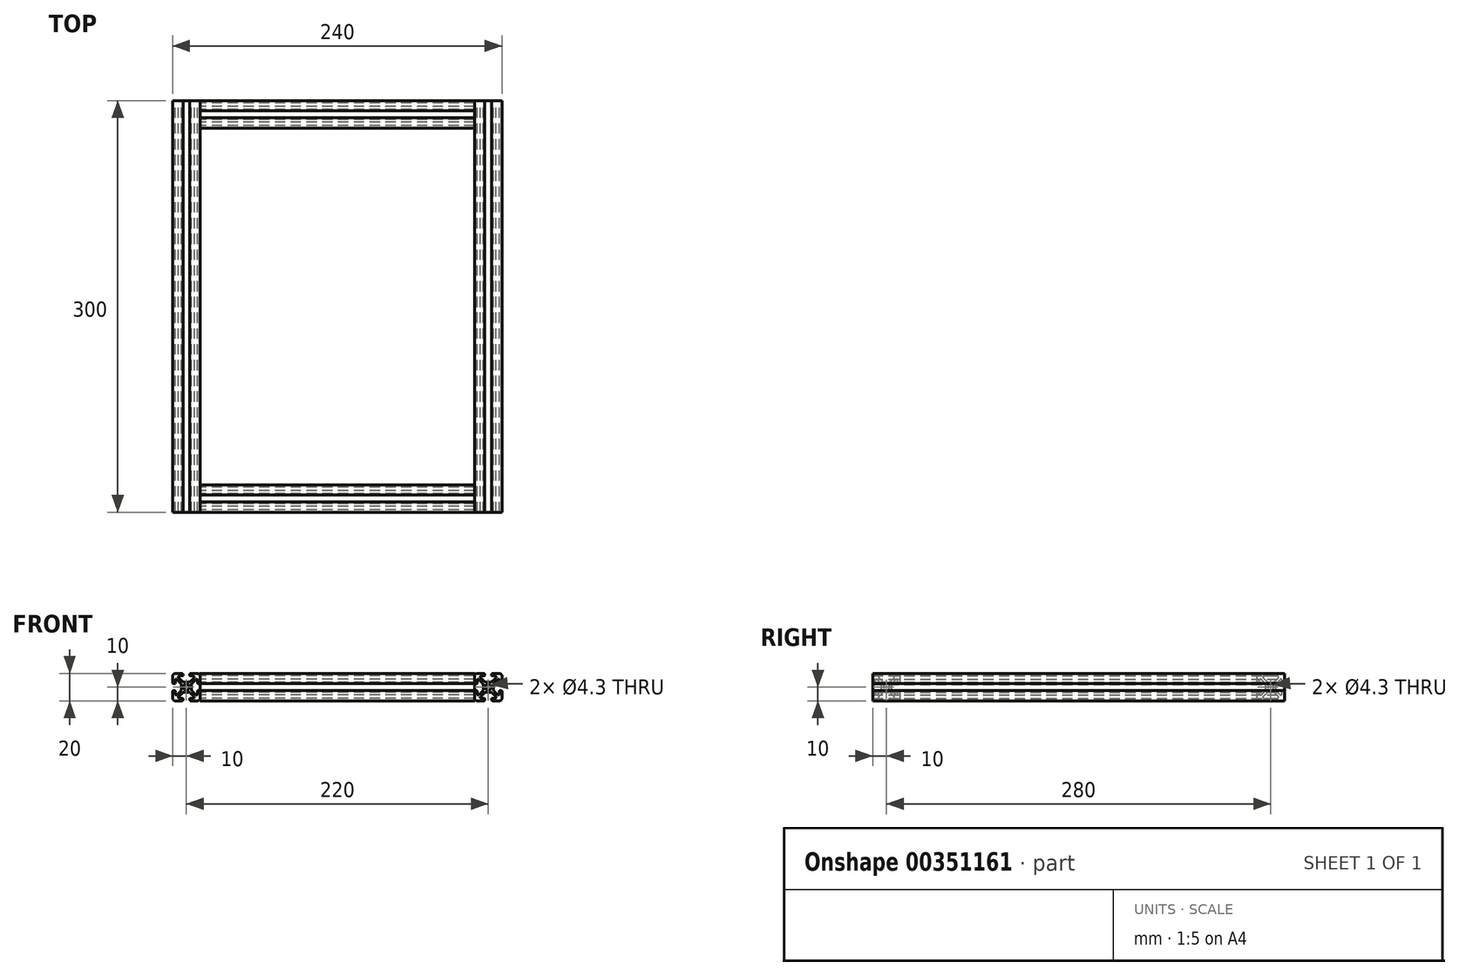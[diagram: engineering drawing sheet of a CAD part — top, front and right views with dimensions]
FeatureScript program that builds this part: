
annotation { "Feature Type Name" : "Feature", "Feature Type Description" : "" }
export const myFeature = defineFeature(function(context is Context, id is Id, definition is map)
    precondition{}
    {
        {
            var Q0;
            Q0=qCreatedBy(makeId("Front.planeOp"),FACE);
            var sketch = newSketch(context, id + "F0", { "sketchPlane" : qUnion([Q0])});
            skLineSegment(sketch, "E0", {"start": v(-103.22, -5.5) * mm, "end": v(-105.47, -3.26) * mm});
            skLineSegment(sketch, "E1", {"start": v(-114.53, 3.26) * mm, "end": v(-116.78, 5.5) * mm});
            skLineSegment(sketch, "E2", {"start": v(-104.5, -6.78) * mm, "end": v(-106.74, -4.53) * mm});
            skLineSegment(sketch, "E3", {"start": v(-113.26, 4.53) * mm, "end": v(-115.5, 6.78) * mm});
            skLineSegment(sketch, "E4", {"start": v(-106.7, -10) * mm, "end": v(-102, -10) * mm});
            skLineSegment(sketch, "E5", {"start": v(-118, -10) * mm, "end": v(-113.3, -10) * mm});
            skLineSegment(sketch, "E6", {"start": v(-114.92, -8.2) * mm, "end": v(-112.8, -8.2) * mm});
            skLineSegment(sketch, "E7", {"start": v(-107.2, -8.2) * mm, "end": v(-105.08, -8.2) * mm});
            skLineSegment(sketch, "E8", {"start": v(-111.13, -3.65) * mm, "end": v(-108.87, -3.65) * mm});
            skLineSegment(sketch, "E9", {"start": v(-101.5, -2.5) * mm, "end": v(-100.8, -2.5) * mm});
            skLineSegment(sketch, "E10", {"start": v(-119.2, -2.5) * mm, "end": v(-118.5, -2.5) * mm});
            skLineSegment(sketch, "E11", {"start": v(-101.5, 2.5) * mm, "end": v(-100.8, 2.5) * mm});
            skLineSegment(sketch, "E12", {"start": v(-119.2, 2.5) * mm, "end": v(-118.5, 2.5) * mm});
            skLineSegment(sketch, "E13", {"start": v(-111.13, 3.65) * mm, "end": v(-108.87, 3.65) * mm});
            skLineSegment(sketch, "E14", {"start": v(-107.2, 8.2) * mm, "end": v(-105.08, 8.2) * mm});
            skLineSegment(sketch, "E15", {"start": v(-114.92, 8.2) * mm, "end": v(-112.8, 8.2) * mm});
            skLineSegment(sketch, "E16", {"start": v(-106.7, 10) * mm, "end": v(-102, 10) * mm});
            skLineSegment(sketch, "E17", {"start": v(-118, 10) * mm, "end": v(-113.3, 10) * mm});
            skLineSegment(sketch, "E18", {"start": v(-105.47, 3.26) * mm, "end": v(-103.22, 5.5) * mm});
            skLineSegment(sketch, "E19", {"start": v(-115.5, -6.78) * mm, "end": v(-113.26, -4.53) * mm});
            skLineSegment(sketch, "E20", {"start": v(-106.74, 4.53) * mm, "end": v(-104.5, 6.78) * mm});
            skLineSegment(sketch, "E21", {"start": v(-116.78, -5.5) * mm, "end": v(-114.53, -3.26) * mm});
            skLineSegment(sketch, "E22", {"start": v(-120, 3.3) * mm, "end": v(-120, 8) * mm});
            skLineSegment(sketch, "E23", {"start": v(-120, -8) * mm, "end": v(-120, -3.3) * mm});
            skLineSegment(sketch, "E24", {"start": v(-118.2, 2.8) * mm, "end": v(-118.2, 4.92) * mm});
            skLineSegment(sketch, "E25", {"start": v(-118.2, -4.92) * mm, "end": v(-118.2, -2.8) * mm});
            skLineSegment(sketch, "E26", {"start": v(-113.65, -1.13) * mm, "end": v(-113.65, 1.13) * mm});
            skLineSegment(sketch, "E27", {"start": v(-112.5, 8.5) * mm, "end": v(-112.5, 9.2) * mm});
            skLineSegment(sketch, "E28", {"start": v(-112.5, -9.2) * mm, "end": v(-112.5, -8.5) * mm});
            skLineSegment(sketch, "E29", {"start": v(-107.5, -9.2) * mm, "end": v(-107.5, -8.5) * mm});
            skLineSegment(sketch, "E30", {"start": v(-107.5, 8.5) * mm, "end": v(-107.5, 9.2) * mm});
            skLineSegment(sketch, "E31", {"start": v(-106.35, -1.13) * mm, "end": v(-106.35, 1.13) * mm});
            skLineSegment(sketch, "E32", {"start": v(-101.8, -4.92) * mm, "end": v(-101.8, -2.8) * mm});
            skLineSegment(sketch, "E33", {"start": v(-101.8, 2.8) * mm, "end": v(-101.8, 4.92) * mm});
            skLineSegment(sketch, "E34", {"start": v(-100, -8) * mm, "end": v(-100, -3.3) * mm});
            skLineSegment(sketch, "E35", {"start": v(-100, 3.3) * mm, "end": v(-100, 8) * mm});
            skArc(sketch, "E36", {"start": v(-119.2, -2.5) * mm, "mid": v(-119.77, -2.73) * mm, "end": v(-120, -3.3) * mm});
            skArc(sketch, "E37", {"start": v(-120, 3.3) * mm, "mid": v(-119.77, 2.73) * mm, "end": v(-119.2, 2.5) * mm});
            skArc(sketch, "E38", {"start": v(-118.2, -2.8) * mm, "mid": v(-118.29, -2.59) * mm, "end": v(-118.5, -2.5) * mm});
            skArc(sketch, "E39", {"start": v(-118.5, 2.5) * mm, "mid": v(-118.29, 2.59) * mm, "end": v(-118.2, 2.8) * mm});
            skArc(sketch, "E40", {"start": v(-120, -8) * mm, "mid": v(-119.41, -9.41) * mm, "end": v(-118, -10) * mm});
            skArc(sketch, "E41", {"start": v(-118, 10) * mm, "mid": v(-119.41, 9.41) * mm, "end": v(-120, 8) * mm});
            skArc(sketch, "E42", {"start": v(-118.2, -4.92) * mm, "mid": v(-117.69, -5.69) * mm, "end": v(-116.78, -5.5) * mm});
            skArc(sketch, "E43", {"start": v(-116.78, 5.5) * mm, "mid": v(-117.69, 5.69) * mm, "end": v(-118.2, 4.92) * mm});
            skArc(sketch, "E44", {"start": v(-114.53, -3.26) * mm, "mid": v(-113.88, -2.28) * mm, "end": v(-113.65, -1.13) * mm});
            skArc(sketch, "E45", {"start": v(-113.65, 1.13) * mm, "mid": v(-113.88, 2.28) * mm, "end": v(-114.53, 3.26) * mm});
            skArc(sketch, "E46", {"start": v(-115.5, -6.78) * mm, "mid": v(-115.69, -7.69) * mm, "end": v(-114.92, -8.2) * mm});
            skArc(sketch, "E47", {"start": v(-114.92, 8.2) * mm, "mid": v(-115.69, 7.69) * mm, "end": v(-115.5, 6.78) * mm});
            skArc(sketch, "E48", {"start": v(-113.3, -10) * mm, "mid": v(-112.73, -9.77) * mm, "end": v(-112.5, -9.2) * mm});
            skArc(sketch, "E49", {"start": v(-112.5, 9.2) * mm, "mid": v(-112.73, 9.77) * mm, "end": v(-113.3, 10) * mm});
            skArc(sketch, "E50", {"start": v(-112.5, -8.5) * mm, "mid": v(-112.59, -8.29) * mm, "end": v(-112.8, -8.2) * mm});
            skArc(sketch, "E51", {"start": v(-112.8, 8.2) * mm, "mid": v(-112.59, 8.29) * mm, "end": v(-112.5, 8.5) * mm});
            skArc(sketch, "E52", {"start": v(-111.13, -3.65) * mm, "mid": v(-112.28, -3.88) * mm, "end": v(-113.26, -4.53) * mm});
            skArc(sketch, "E53", {"start": v(-113.26, 4.53) * mm, "mid": v(-112.28, 3.88) * mm, "end": v(-111.13, 3.65) * mm});
            skCircle(sketch, "E54", {"center": v(-110, 0) * mm, "radius": 2.15 * mm});
            skArc(sketch, "E55", {"start": v(-106.74, -4.53) * mm, "mid": v(-107.72, -3.88) * mm, "end": v(-108.87, -3.65) * mm});
            skArc(sketch, "E56", {"start": v(-108.87, 3.65) * mm, "mid": v(-107.72, 3.88) * mm, "end": v(-106.74, 4.53) * mm});
            skArc(sketch, "E57", {"start": v(-107.2, -8.2) * mm, "mid": v(-107.41, -8.29) * mm, "end": v(-107.5, -8.5) * mm});
            skArc(sketch, "E58", {"start": v(-107.5, 8.5) * mm, "mid": v(-107.41, 8.29) * mm, "end": v(-107.2, 8.2) * mm});
            skArc(sketch, "E59", {"start": v(-107.5, -9.2) * mm, "mid": v(-107.27, -9.77) * mm, "end": v(-106.7, -10) * mm});
            skArc(sketch, "E60", {"start": v(-106.7, 10) * mm, "mid": v(-107.27, 9.77) * mm, "end": v(-107.5, 9.2) * mm});
            skArc(sketch, "E61", {"start": v(-105.08, -8.2) * mm, "mid": v(-104.31, -7.69) * mm, "end": v(-104.5, -6.78) * mm});
            skArc(sketch, "E62", {"start": v(-104.5, 6.78) * mm, "mid": v(-104.31, 7.69) * mm, "end": v(-105.08, 8.2) * mm});
            skArc(sketch, "E63", {"start": v(-106.35, -1.13) * mm, "mid": v(-106.12, -2.28) * mm, "end": v(-105.47, -3.26) * mm});
            skArc(sketch, "E64", {"start": v(-105.47, 3.26) * mm, "mid": v(-106.12, 2.28) * mm, "end": v(-106.35, 1.13) * mm});
            skArc(sketch, "E65", {"start": v(-103.22, -5.5) * mm, "mid": v(-102.31, -5.69) * mm, "end": v(-101.8, -4.92) * mm});
            skArc(sketch, "E66", {"start": v(-101.8, 4.92) * mm, "mid": v(-102.31, 5.69) * mm, "end": v(-103.22, 5.5) * mm});
            skArc(sketch, "E67", {"start": v(-102, -10) * mm, "mid": v(-100.59, -9.41) * mm, "end": v(-100, -8) * mm});
            skArc(sketch, "E68", {"start": v(-100, 8) * mm, "mid": v(-100.59, 9.41) * mm, "end": v(-102, 10) * mm});
            skArc(sketch, "E69", {"start": v(-101.5, -2.5) * mm, "mid": v(-101.71, -2.59) * mm, "end": v(-101.8, -2.8) * mm});
            skArc(sketch, "E70", {"start": v(-101.8, 2.8) * mm, "mid": v(-101.71, 2.59) * mm, "end": v(-101.5, 2.5) * mm});
            skArc(sketch, "E71", {"start": v(-100, -3.3) * mm, "mid": v(-100.23, -2.73) * mm, "end": v(-100.8, -2.5) * mm});
            skArc(sketch, "E72", {"start": v(-100.8, 2.5) * mm, "mid": v(-100.23, 2.73) * mm, "end": v(-100, 3.3) * mm});
            skLineSegment(sketch, "E73", {"start": v(-110, 10) * mm, "end": v(-110, -10) * mm});
            skLineSegment(sketch, "E74", {"start": v(-120, 0) * mm, "end": v(-100, 0) * mm});
            skLineSegment(sketch, "E75", {"start": v(116.78, -5.5) * mm, "end": v(114.53, -3.26) * mm});
            skLineSegment(sketch, "E76", {"start": v(105.47, 3.26) * mm, "end": v(103.22, 5.5) * mm});
            skLineSegment(sketch, "E77", {"start": v(115.5, -6.78) * mm, "end": v(113.26, -4.53) * mm});
            skLineSegment(sketch, "E78", {"start": v(106.74, 4.53) * mm, "end": v(104.5, 6.78) * mm});
            skLineSegment(sketch, "E79", {"start": v(113.3, -10) * mm, "end": v(118, -10) * mm});
            skLineSegment(sketch, "E80", {"start": v(102, -10) * mm, "end": v(106.7, -10) * mm});
            skLineSegment(sketch, "E81", {"start": v(105.08, -8.2) * mm, "end": v(107.2, -8.2) * mm});
            skLineSegment(sketch, "E82", {"start": v(112.8, -8.2) * mm, "end": v(114.92, -8.2) * mm});
            skLineSegment(sketch, "E83", {"start": v(108.87, -3.65) * mm, "end": v(111.13, -3.65) * mm});
            skLineSegment(sketch, "E84", {"start": v(118.5, -2.5) * mm, "end": v(119.2, -2.5) * mm});
            skLineSegment(sketch, "E85", {"start": v(100.8, -2.5) * mm, "end": v(101.5, -2.5) * mm});
            skLineSegment(sketch, "E86", {"start": v(118.5, 2.5) * mm, "end": v(119.2, 2.5) * mm});
            skLineSegment(sketch, "E87", {"start": v(100.8, 2.5) * mm, "end": v(101.5, 2.5) * mm});
            skLineSegment(sketch, "E88", {"start": v(108.87, 3.65) * mm, "end": v(111.13, 3.65) * mm});
            skLineSegment(sketch, "E89", {"start": v(112.8, 8.2) * mm, "end": v(114.92, 8.2) * mm});
            skLineSegment(sketch, "E90", {"start": v(105.08, 8.2) * mm, "end": v(107.2, 8.2) * mm});
            skLineSegment(sketch, "E91", {"start": v(113.3, 10) * mm, "end": v(118, 10) * mm});
            skLineSegment(sketch, "E92", {"start": v(102, 10) * mm, "end": v(106.7, 10) * mm});
            skLineSegment(sketch, "E93", {"start": v(114.53, 3.26) * mm, "end": v(116.78, 5.5) * mm});
            skLineSegment(sketch, "E94", {"start": v(104.5, -6.78) * mm, "end": v(106.74, -4.53) * mm});
            skLineSegment(sketch, "E95", {"start": v(113.26, 4.53) * mm, "end": v(115.5, 6.78) * mm});
            skLineSegment(sketch, "E96", {"start": v(103.22, -5.5) * mm, "end": v(105.47, -3.26) * mm});
            skLineSegment(sketch, "E97", {"start": v(100, 3.3) * mm, "end": v(100, 8) * mm});
            skLineSegment(sketch, "E98", {"start": v(100, -8) * mm, "end": v(100, -3.3) * mm});
            skLineSegment(sketch, "E99", {"start": v(101.8, 2.8) * mm, "end": v(101.8, 4.92) * mm});
            skLineSegment(sketch, "E100", {"start": v(101.8, -4.92) * mm, "end": v(101.8, -2.8) * mm});
            skLineSegment(sketch, "E101", {"start": v(106.35, -1.13) * mm, "end": v(106.35, 1.13) * mm});
            skLineSegment(sketch, "E102", {"start": v(107.5, 8.5) * mm, "end": v(107.5, 9.2) * mm});
            skLineSegment(sketch, "E103", {"start": v(107.5, -9.2) * mm, "end": v(107.5, -8.5) * mm});
            skLineSegment(sketch, "E104", {"start": v(112.5, -9.2) * mm, "end": v(112.5, -8.5) * mm});
            skLineSegment(sketch, "E105", {"start": v(112.5, 8.5) * mm, "end": v(112.5, 9.2) * mm});
            skLineSegment(sketch, "E106", {"start": v(113.65, -1.13) * mm, "end": v(113.65, 1.13) * mm});
            skLineSegment(sketch, "E107", {"start": v(118.2, -4.92) * mm, "end": v(118.2, -2.8) * mm});
            skLineSegment(sketch, "E108", {"start": v(118.2, 2.8) * mm, "end": v(118.2, 4.92) * mm});
            skLineSegment(sketch, "E109", {"start": v(120, -8) * mm, "end": v(120, -3.3) * mm});
            skLineSegment(sketch, "E110", {"start": v(120, 3.3) * mm, "end": v(120, 8) * mm});
            skArc(sketch, "E111", {"start": v(100.8, -2.5) * mm, "mid": v(100.23, -2.73) * mm, "end": v(100, -3.3) * mm});
            skArc(sketch, "E112", {"start": v(100, 3.3) * mm, "mid": v(100.23, 2.73) * mm, "end": v(100.8, 2.5) * mm});
            skArc(sketch, "E113", {"start": v(101.8, -2.8) * mm, "mid": v(101.71, -2.59) * mm, "end": v(101.5, -2.5) * mm});
            skArc(sketch, "E114", {"start": v(101.5, 2.5) * mm, "mid": v(101.71, 2.59) * mm, "end": v(101.8, 2.8) * mm});
            skArc(sketch, "E115", {"start": v(100, -8) * mm, "mid": v(100.59, -9.41) * mm, "end": v(102, -10) * mm});
            skArc(sketch, "E116", {"start": v(102, 10) * mm, "mid": v(100.59, 9.41) * mm, "end": v(100, 8) * mm});
            skArc(sketch, "E117", {"start": v(101.8, -4.92) * mm, "mid": v(102.31, -5.69) * mm, "end": v(103.22, -5.5) * mm});
            skArc(sketch, "E118", {"start": v(103.22, 5.5) * mm, "mid": v(102.31, 5.69) * mm, "end": v(101.8, 4.92) * mm});
            skArc(sketch, "E119", {"start": v(105.47, -3.26) * mm, "mid": v(106.12, -2.28) * mm, "end": v(106.35, -1.13) * mm});
            skArc(sketch, "E120", {"start": v(106.35, 1.13) * mm, "mid": v(106.12, 2.28) * mm, "end": v(105.47, 3.26) * mm});
            skArc(sketch, "E121", {"start": v(104.5, -6.78) * mm, "mid": v(104.31, -7.69) * mm, "end": v(105.08, -8.2) * mm});
            skArc(sketch, "E122", {"start": v(105.08, 8.2) * mm, "mid": v(104.31, 7.69) * mm, "end": v(104.5, 6.78) * mm});
            skArc(sketch, "E123", {"start": v(106.7, -10) * mm, "mid": v(107.27, -9.77) * mm, "end": v(107.5, -9.2) * mm});
            skArc(sketch, "E124", {"start": v(107.5, 9.2) * mm, "mid": v(107.27, 9.77) * mm, "end": v(106.7, 10) * mm});
            skArc(sketch, "E125", {"start": v(107.5, -8.5) * mm, "mid": v(107.41, -8.29) * mm, "end": v(107.2, -8.2) * mm});
            skArc(sketch, "E126", {"start": v(107.2, 8.2) * mm, "mid": v(107.41, 8.29) * mm, "end": v(107.5, 8.5) * mm});
            skArc(sketch, "E127", {"start": v(108.87, -3.65) * mm, "mid": v(107.72, -3.88) * mm, "end": v(106.74, -4.53) * mm});
            skArc(sketch, "E128", {"start": v(106.74, 4.53) * mm, "mid": v(107.72, 3.88) * mm, "end": v(108.87, 3.65) * mm});
            skCircle(sketch, "E129", {"center": v(110, 0) * mm, "radius": 2.15 * mm});
            skArc(sketch, "E130", {"start": v(113.26, -4.53) * mm, "mid": v(112.28, -3.88) * mm, "end": v(111.13, -3.65) * mm});
            skArc(sketch, "E131", {"start": v(111.13, 3.65) * mm, "mid": v(112.28, 3.88) * mm, "end": v(113.26, 4.53) * mm});
            skArc(sketch, "E132", {"start": v(112.8, -8.2) * mm, "mid": v(112.59, -8.29) * mm, "end": v(112.5, -8.5) * mm});
            skArc(sketch, "E133", {"start": v(112.5, 8.5) * mm, "mid": v(112.59, 8.29) * mm, "end": v(112.8, 8.2) * mm});
            skArc(sketch, "E134", {"start": v(112.5, -9.2) * mm, "mid": v(112.73, -9.77) * mm, "end": v(113.3, -10) * mm});
            skArc(sketch, "E135", {"start": v(113.3, 10) * mm, "mid": v(112.73, 9.77) * mm, "end": v(112.5, 9.2) * mm});
            skArc(sketch, "E136", {"start": v(114.92, -8.2) * mm, "mid": v(115.69, -7.69) * mm, "end": v(115.5, -6.78) * mm});
            skArc(sketch, "E137", {"start": v(115.5, 6.78) * mm, "mid": v(115.69, 7.69) * mm, "end": v(114.92, 8.2) * mm});
            skArc(sketch, "E138", {"start": v(113.65, -1.13) * mm, "mid": v(113.88, -2.28) * mm, "end": v(114.53, -3.26) * mm});
            skArc(sketch, "E139", {"start": v(114.53, 3.26) * mm, "mid": v(113.88, 2.28) * mm, "end": v(113.65, 1.13) * mm});
            skArc(sketch, "E140", {"start": v(116.78, -5.5) * mm, "mid": v(117.69, -5.69) * mm, "end": v(118.2, -4.92) * mm});
            skArc(sketch, "E141", {"start": v(118.2, 4.92) * mm, "mid": v(117.69, 5.69) * mm, "end": v(116.78, 5.5) * mm});
            skArc(sketch, "E142", {"start": v(118, -10) * mm, "mid": v(119.41, -9.41) * mm, "end": v(120, -8) * mm});
            skArc(sketch, "E143", {"start": v(120, 8) * mm, "mid": v(119.41, 9.41) * mm, "end": v(118, 10) * mm});
            skArc(sketch, "E144", {"start": v(118.5, -2.5) * mm, "mid": v(118.29, -2.59) * mm, "end": v(118.2, -2.8) * mm});
            skArc(sketch, "E145", {"start": v(118.2, 2.8) * mm, "mid": v(118.29, 2.59) * mm, "end": v(118.5, 2.5) * mm});
            skArc(sketch, "E146", {"start": v(120, -3.3) * mm, "mid": v(119.77, -2.73) * mm, "end": v(119.2, -2.5) * mm});
            skArc(sketch, "E147", {"start": v(119.2, 2.5) * mm, "mid": v(119.77, 2.73) * mm, "end": v(120, 3.3) * mm});
            skLineSegment(sketch, "E148", {"start": v(110, 10) * mm, "end": v(110, -10) * mm});
            skLineSegment(sketch, "E149", {"start": v(100, 0) * mm, "end": v(120, 0) * mm});
            skSolve(sketch);
        }
        {
            var Q0;
            Q0=makeQuery(id+"F0.imprint","IMPRINT",FACE,{"disambiguationData":[TD([[makeQuery(id+"F0.imprint","IMPRINT",EDGE,{"derivedFrom":sQuery(id+"F0.wireOp",EDGE,"E1")}),-1.0]])]});
            var Q1;
            Q1=makeQuery(id+"F0.imprint","IMPRINT",FACE,{"disambiguationData":[TD([[makeQuery(id+"F0.imprint","IMPRINT",EDGE,{"derivedFrom":sQuery(id+"F0.wireOp",EDGE,"E11")}),1.0]])]});
            var Q2;
            Q2=makeQuery(id+"F0.imprint","IMPRINT",FACE,{"disambiguationData":[TD([[makeQuery(id+"F0.imprint","IMPRINT",EDGE,{"derivedFrom":sQuery(id+"F0.wireOp",EDGE,"E5")}),1.0]])]});
            var Q3;
            Q3=makeQuery(id+"F0.imprint","IMPRINT",FACE,{"disambiguationData":[TD([[makeQuery(id+"F0.imprint","IMPRINT",EDGE,{"derivedFrom":sQuery(id+"F0.wireOp",EDGE,"E0")}),1.0]])]});
            var Q4;
            Q4=makeQuery(id+"F0.imprint","IMPRINT",FACE,{"disambiguationData":[TD([[makeQuery(id+"F0.imprint","IMPRINT",EDGE,{"derivedFrom":sQuery(id+"F0.wireOp",EDGE,"E76")}),-1.0]])]});
            var Q5;
            Q5=makeQuery(id+"F0.imprint","IMPRINT",FACE,{"disambiguationData":[TD([[makeQuery(id+"F0.imprint","IMPRINT",EDGE,{"derivedFrom":sQuery(id+"F0.wireOp",EDGE,"E86")}),1.0]])]});
            var Q6;
            Q6=makeQuery(id+"F0.imprint","IMPRINT",FACE,{"disambiguationData":[TD([[makeQuery(id+"F0.imprint","IMPRINT",EDGE,{"derivedFrom":sQuery(id+"F0.wireOp",EDGE,"E75")}),1.0]])]});
            var Q7;
            Q7=makeQuery(id+"F0.imprint","IMPRINT",FACE,{"disambiguationData":[TD([[makeQuery(id+"F0.imprint","IMPRINT",EDGE,{"derivedFrom":sQuery(id+"F0.wireOp",EDGE,"E80")}),1.0]])]});
            extrude(context, id + "F1", {"entities" : qUnion([Q0, Q1, Q2, Q3, Q4, Q5, Q6, Q7]), "endBound" : BoundingType.SYMMETRIC, "depth" : 300 * mm});
        }
        {
            var Q0;
            Q0=qCreatedBy(makeId("Right.planeOp"),FACE);
            var sketch = newSketch(context, id + "F2", { "sketchPlane" : qUnion([Q0])});
            skLineSegment(sketch, "E150", {"start": v(-133.22, -5.5) * mm, "end": v(-135.47, -3.26) * mm});
            skLineSegment(sketch, "E151", {"start": v(-144.53, 3.26) * mm, "end": v(-146.78, 5.5) * mm});
            skLineSegment(sketch, "E152", {"start": v(-134.5, -6.78) * mm, "end": v(-136.74, -4.53) * mm});
            skLineSegment(sketch, "E153", {"start": v(-143.26, 4.53) * mm, "end": v(-145.5, 6.78) * mm});
            skLineSegment(sketch, "E154", {"start": v(-136.7, -10) * mm, "end": v(-132, -10) * mm});
            skLineSegment(sketch, "E155", {"start": v(-148, -10) * mm, "end": v(-143.3, -10) * mm});
            skLineSegment(sketch, "E156", {"start": v(-144.92, -8.2) * mm, "end": v(-142.8, -8.2) * mm});
            skLineSegment(sketch, "E157", {"start": v(-137.2, -8.2) * mm, "end": v(-135.08, -8.2) * mm});
            skLineSegment(sketch, "E158", {"start": v(-141.13, -3.65) * mm, "end": v(-138.87, -3.65) * mm});
            skLineSegment(sketch, "E159", {"start": v(-131.5, -2.5) * mm, "end": v(-130.8, -2.5) * mm});
            skLineSegment(sketch, "E160", {"start": v(-149.2, -2.5) * mm, "end": v(-148.5, -2.5) * mm});
            skLineSegment(sketch, "E161", {"start": v(-131.5, 2.5) * mm, "end": v(-130.8, 2.5) * mm});
            skLineSegment(sketch, "E162", {"start": v(-149.2, 2.5) * mm, "end": v(-148.5, 2.5) * mm});
            skLineSegment(sketch, "E163", {"start": v(-141.13, 3.65) * mm, "end": v(-138.87, 3.65) * mm});
            skLineSegment(sketch, "E164", {"start": v(-137.2, 8.2) * mm, "end": v(-135.08, 8.2) * mm});
            skLineSegment(sketch, "E165", {"start": v(-144.92, 8.2) * mm, "end": v(-142.8, 8.2) * mm});
            skLineSegment(sketch, "E166", {"start": v(-136.7, 10) * mm, "end": v(-132, 10) * mm});
            skLineSegment(sketch, "E167", {"start": v(-148, 10) * mm, "end": v(-143.3, 10) * mm});
            skLineSegment(sketch, "E168", {"start": v(-135.47, 3.26) * mm, "end": v(-133.22, 5.5) * mm});
            skLineSegment(sketch, "E169", {"start": v(-145.5, -6.78) * mm, "end": v(-143.26, -4.53) * mm});
            skLineSegment(sketch, "E170", {"start": v(-136.74, 4.53) * mm, "end": v(-134.5, 6.78) * mm});
            skLineSegment(sketch, "E171", {"start": v(-146.78, -5.5) * mm, "end": v(-144.53, -3.26) * mm});
            skLineSegment(sketch, "E172", {"start": v(-150, 3.3) * mm, "end": v(-150, 8) * mm});
            skLineSegment(sketch, "E173", {"start": v(-150, -8) * mm, "end": v(-150, -3.3) * mm});
            skLineSegment(sketch, "E174", {"start": v(-148.2, 2.8) * mm, "end": v(-148.2, 4.92) * mm});
            skLineSegment(sketch, "E175", {"start": v(-148.2, -4.92) * mm, "end": v(-148.2, -2.8) * mm});
            skLineSegment(sketch, "E176", {"start": v(-143.65, -1.13) * mm, "end": v(-143.65, 1.13) * mm});
            skLineSegment(sketch, "E177", {"start": v(-142.5, 8.5) * mm, "end": v(-142.5, 9.2) * mm});
            skLineSegment(sketch, "E178", {"start": v(-142.5, -9.2) * mm, "end": v(-142.5, -8.5) * mm});
            skLineSegment(sketch, "E179", {"start": v(-137.5, -9.2) * mm, "end": v(-137.5, -8.5) * mm});
            skLineSegment(sketch, "E180", {"start": v(-137.5, 8.5) * mm, "end": v(-137.5, 9.2) * mm});
            skLineSegment(sketch, "E181", {"start": v(-136.35, -1.13) * mm, "end": v(-136.35, 1.13) * mm});
            skLineSegment(sketch, "E182", {"start": v(-131.8, -4.92) * mm, "end": v(-131.8, -2.8) * mm});
            skLineSegment(sketch, "E183", {"start": v(-131.8, 2.8) * mm, "end": v(-131.8, 4.92) * mm});
            skLineSegment(sketch, "E184", {"start": v(-130, -8) * mm, "end": v(-130, -3.3) * mm});
            skLineSegment(sketch, "E185", {"start": v(-130, 3.3) * mm, "end": v(-130, 8) * mm});
            skArc(sketch, "E186", {"start": v(-149.2, -2.5) * mm, "mid": v(-149.77, -2.73) * mm, "end": v(-150, -3.3) * mm});
            skArc(sketch, "E187", {"start": v(-150, 3.3) * mm, "mid": v(-149.77, 2.73) * mm, "end": v(-149.2, 2.5) * mm});
            skArc(sketch, "E188", {"start": v(-148.2, -2.8) * mm, "mid": v(-148.29, -2.59) * mm, "end": v(-148.5, -2.5) * mm});
            skArc(sketch, "E189", {"start": v(-148.5, 2.5) * mm, "mid": v(-148.29, 2.59) * mm, "end": v(-148.2, 2.8) * mm});
            skArc(sketch, "E190", {"start": v(-150, -8) * mm, "mid": v(-149.41, -9.41) * mm, "end": v(-148, -10) * mm});
            skArc(sketch, "E191", {"start": v(-148, 10) * mm, "mid": v(-149.41, 9.41) * mm, "end": v(-150, 8) * mm});
            skArc(sketch, "E192", {"start": v(-148.2, -4.92) * mm, "mid": v(-147.69, -5.69) * mm, "end": v(-146.78, -5.5) * mm});
            skArc(sketch, "E193", {"start": v(-146.78, 5.5) * mm, "mid": v(-147.69, 5.69) * mm, "end": v(-148.2, 4.92) * mm});
            skArc(sketch, "E194", {"start": v(-144.53, -3.26) * mm, "mid": v(-143.88, -2.28) * mm, "end": v(-143.65, -1.13) * mm});
            skArc(sketch, "E195", {"start": v(-143.65, 1.13) * mm, "mid": v(-143.88, 2.28) * mm, "end": v(-144.53, 3.26) * mm});
            skArc(sketch, "E196", {"start": v(-145.5, -6.78) * mm, "mid": v(-145.69, -7.69) * mm, "end": v(-144.92, -8.2) * mm});
            skArc(sketch, "E197", {"start": v(-144.92, 8.2) * mm, "mid": v(-145.69, 7.69) * mm, "end": v(-145.5, 6.78) * mm});
            skArc(sketch, "E198", {"start": v(-143.3, -10) * mm, "mid": v(-142.73, -9.77) * mm, "end": v(-142.5, -9.2) * mm});
            skArc(sketch, "E199", {"start": v(-142.5, 9.2) * mm, "mid": v(-142.73, 9.77) * mm, "end": v(-143.3, 10) * mm});
            skArc(sketch, "E200", {"start": v(-142.5, -8.5) * mm, "mid": v(-142.59, -8.29) * mm, "end": v(-142.8, -8.2) * mm});
            skArc(sketch, "E201", {"start": v(-142.8, 8.2) * mm, "mid": v(-142.59, 8.29) * mm, "end": v(-142.5, 8.5) * mm});
            skArc(sketch, "E202", {"start": v(-141.13, -3.65) * mm, "mid": v(-142.28, -3.88) * mm, "end": v(-143.26, -4.53) * mm});
            skArc(sketch, "E203", {"start": v(-143.26, 4.53) * mm, "mid": v(-142.28, 3.88) * mm, "end": v(-141.13, 3.65) * mm});
            skCircle(sketch, "E204", {"center": v(-140, 0) * mm, "radius": 2.15 * mm});
            skArc(sketch, "E205", {"start": v(-136.74, -4.53) * mm, "mid": v(-137.72, -3.88) * mm, "end": v(-138.87, -3.65) * mm});
            skArc(sketch, "E206", {"start": v(-138.87, 3.65) * mm, "mid": v(-137.72, 3.88) * mm, "end": v(-136.74, 4.53) * mm});
            skArc(sketch, "E207", {"start": v(-137.2, -8.2) * mm, "mid": v(-137.41, -8.29) * mm, "end": v(-137.5, -8.5) * mm});
            skArc(sketch, "E208", {"start": v(-137.5, 8.5) * mm, "mid": v(-137.41, 8.29) * mm, "end": v(-137.2, 8.2) * mm});
            skArc(sketch, "E209", {"start": v(-137.5, -9.2) * mm, "mid": v(-137.27, -9.77) * mm, "end": v(-136.7, -10) * mm});
            skArc(sketch, "E210", {"start": v(-136.7, 10) * mm, "mid": v(-137.27, 9.77) * mm, "end": v(-137.5, 9.2) * mm});
            skArc(sketch, "E211", {"start": v(-135.08, -8.2) * mm, "mid": v(-134.31, -7.69) * mm, "end": v(-134.5, -6.78) * mm});
            skArc(sketch, "E212", {"start": v(-134.5, 6.78) * mm, "mid": v(-134.31, 7.69) * mm, "end": v(-135.08, 8.2) * mm});
            skArc(sketch, "E213", {"start": v(-136.35, -1.13) * mm, "mid": v(-136.12, -2.28) * mm, "end": v(-135.47, -3.26) * mm});
            skArc(sketch, "E214", {"start": v(-135.47, 3.26) * mm, "mid": v(-136.12, 2.28) * mm, "end": v(-136.35, 1.13) * mm});
            skArc(sketch, "E215", {"start": v(-133.22, -5.5) * mm, "mid": v(-132.31, -5.69) * mm, "end": v(-131.8, -4.92) * mm});
            skArc(sketch, "E216", {"start": v(-131.8, 4.92) * mm, "mid": v(-132.31, 5.69) * mm, "end": v(-133.22, 5.5) * mm});
            skArc(sketch, "E217", {"start": v(-132, -10) * mm, "mid": v(-130.59, -9.41) * mm, "end": v(-130, -8) * mm});
            skArc(sketch, "E218", {"start": v(-130, 8) * mm, "mid": v(-130.59, 9.41) * mm, "end": v(-132, 10) * mm});
            skArc(sketch, "E219", {"start": v(-131.5, -2.5) * mm, "mid": v(-131.71, -2.59) * mm, "end": v(-131.8, -2.8) * mm});
            skArc(sketch, "E220", {"start": v(-131.8, 2.8) * mm, "mid": v(-131.71, 2.59) * mm, "end": v(-131.5, 2.5) * mm});
            skArc(sketch, "E221", {"start": v(-130, -3.3) * mm, "mid": v(-130.23, -2.73) * mm, "end": v(-130.8, -2.5) * mm});
            skArc(sketch, "E222", {"start": v(-130.8, 2.5) * mm, "mid": v(-130.23, 2.73) * mm, "end": v(-130, 3.3) * mm});
            skLineSegment(sketch, "E223", {"start": v(-140, 10) * mm, "end": v(-140, -10) * mm});
            skLineSegment(sketch, "E224", {"start": v(-150, 0) * mm, "end": v(-130, 0) * mm});
            skLineSegment(sketch, "E225", {"start": v(146.78, -5.5) * mm, "end": v(144.53, -3.26) * mm});
            skLineSegment(sketch, "E226", {"start": v(135.47, 3.26) * mm, "end": v(133.22, 5.5) * mm});
            skLineSegment(sketch, "E227", {"start": v(145.5, -6.78) * mm, "end": v(143.26, -4.53) * mm});
            skLineSegment(sketch, "E228", {"start": v(136.74, 4.53) * mm, "end": v(134.5, 6.78) * mm});
            skLineSegment(sketch, "E229", {"start": v(143.3, -10) * mm, "end": v(148, -10) * mm});
            skLineSegment(sketch, "E230", {"start": v(132, -10) * mm, "end": v(136.7, -10) * mm});
            skLineSegment(sketch, "E231", {"start": v(135.08, -8.2) * mm, "end": v(137.2, -8.2) * mm});
            skLineSegment(sketch, "E232", {"start": v(142.8, -8.2) * mm, "end": v(144.92, -8.2) * mm});
            skLineSegment(sketch, "E233", {"start": v(138.87, -3.65) * mm, "end": v(141.13, -3.65) * mm});
            skLineSegment(sketch, "E234", {"start": v(148.5, -2.5) * mm, "end": v(149.2, -2.5) * mm});
            skLineSegment(sketch, "E235", {"start": v(130.8, -2.5) * mm, "end": v(131.5, -2.5) * mm});
            skLineSegment(sketch, "E236", {"start": v(148.5, 2.5) * mm, "end": v(149.2, 2.5) * mm});
            skLineSegment(sketch, "E237", {"start": v(130.8, 2.5) * mm, "end": v(131.5, 2.5) * mm});
            skLineSegment(sketch, "E238", {"start": v(138.87, 3.65) * mm, "end": v(141.13, 3.65) * mm});
            skLineSegment(sketch, "E239", {"start": v(142.8, 8.2) * mm, "end": v(144.92, 8.2) * mm});
            skLineSegment(sketch, "E240", {"start": v(135.08, 8.2) * mm, "end": v(137.2, 8.2) * mm});
            skLineSegment(sketch, "E241", {"start": v(143.3, 10) * mm, "end": v(148, 10) * mm});
            skLineSegment(sketch, "E242", {"start": v(132, 10) * mm, "end": v(136.7, 10) * mm});
            skLineSegment(sketch, "E243", {"start": v(144.53, 3.26) * mm, "end": v(146.78, 5.5) * mm});
            skLineSegment(sketch, "E244", {"start": v(134.5, -6.78) * mm, "end": v(136.74, -4.53) * mm});
            skLineSegment(sketch, "E245", {"start": v(143.26, 4.53) * mm, "end": v(145.5, 6.78) * mm});
            skLineSegment(sketch, "E246", {"start": v(133.22, -5.5) * mm, "end": v(135.47, -3.26) * mm});
            skLineSegment(sketch, "E247", {"start": v(130, 3.3) * mm, "end": v(130, 8) * mm});
            skLineSegment(sketch, "E248", {"start": v(130, -8) * mm, "end": v(130, -3.3) * mm});
            skLineSegment(sketch, "E249", {"start": v(131.8, 2.8) * mm, "end": v(131.8, 4.92) * mm});
            skLineSegment(sketch, "E250", {"start": v(131.8, -4.92) * mm, "end": v(131.8, -2.8) * mm});
            skLineSegment(sketch, "E251", {"start": v(136.35, -1.13) * mm, "end": v(136.35, 1.13) * mm});
            skLineSegment(sketch, "E252", {"start": v(137.5, 8.5) * mm, "end": v(137.5, 9.2) * mm});
            skLineSegment(sketch, "E253", {"start": v(137.5, -9.2) * mm, "end": v(137.5, -8.5) * mm});
            skLineSegment(sketch, "E254", {"start": v(142.5, -9.2) * mm, "end": v(142.5, -8.5) * mm});
            skLineSegment(sketch, "E255", {"start": v(142.5, 8.5) * mm, "end": v(142.5, 9.2) * mm});
            skLineSegment(sketch, "E256", {"start": v(143.65, -1.13) * mm, "end": v(143.65, 1.13) * mm});
            skLineSegment(sketch, "E257", {"start": v(148.2, -4.92) * mm, "end": v(148.2, -2.8) * mm});
            skLineSegment(sketch, "E258", {"start": v(148.2, 2.8) * mm, "end": v(148.2, 4.92) * mm});
            skLineSegment(sketch, "E259", {"start": v(150, -8) * mm, "end": v(150, -3.3) * mm});
            skLineSegment(sketch, "E260", {"start": v(150, 3.3) * mm, "end": v(150, 8) * mm});
            skArc(sketch, "E261", {"start": v(130.8, -2.5) * mm, "mid": v(130.23, -2.73) * mm, "end": v(130, -3.3) * mm});
            skArc(sketch, "E262", {"start": v(130, 3.3) * mm, "mid": v(130.23, 2.73) * mm, "end": v(130.8, 2.5) * mm});
            skArc(sketch, "E263", {"start": v(131.8, -2.8) * mm, "mid": v(131.71, -2.59) * mm, "end": v(131.5, -2.5) * mm});
            skArc(sketch, "E264", {"start": v(131.5, 2.5) * mm, "mid": v(131.71, 2.59) * mm, "end": v(131.8, 2.8) * mm});
            skArc(sketch, "E265", {"start": v(130, -8) * mm, "mid": v(130.59, -9.41) * mm, "end": v(132, -10) * mm});
            skArc(sketch, "E266", {"start": v(132, 10) * mm, "mid": v(130.59, 9.41) * mm, "end": v(130, 8) * mm});
            skArc(sketch, "E267", {"start": v(131.8, -4.92) * mm, "mid": v(132.31, -5.69) * mm, "end": v(133.22, -5.5) * mm});
            skArc(sketch, "E268", {"start": v(133.22, 5.5) * mm, "mid": v(132.31, 5.69) * mm, "end": v(131.8, 4.92) * mm});
            skArc(sketch, "E269", {"start": v(135.47, -3.26) * mm, "mid": v(136.12, -2.28) * mm, "end": v(136.35, -1.13) * mm});
            skArc(sketch, "E270", {"start": v(136.35, 1.13) * mm, "mid": v(136.12, 2.28) * mm, "end": v(135.47, 3.26) * mm});
            skArc(sketch, "E271", {"start": v(134.5, -6.78) * mm, "mid": v(134.31, -7.69) * mm, "end": v(135.08, -8.2) * mm});
            skArc(sketch, "E272", {"start": v(135.08, 8.2) * mm, "mid": v(134.31, 7.69) * mm, "end": v(134.5, 6.78) * mm});
            skArc(sketch, "E273", {"start": v(136.7, -10) * mm, "mid": v(137.27, -9.77) * mm, "end": v(137.5, -9.2) * mm});
            skArc(sketch, "E274", {"start": v(137.5, 9.2) * mm, "mid": v(137.27, 9.77) * mm, "end": v(136.7, 10) * mm});
            skArc(sketch, "E275", {"start": v(137.5, -8.5) * mm, "mid": v(137.41, -8.29) * mm, "end": v(137.2, -8.2) * mm});
            skArc(sketch, "E276", {"start": v(137.2, 8.2) * mm, "mid": v(137.41, 8.29) * mm, "end": v(137.5, 8.5) * mm});
            skArc(sketch, "E277", {"start": v(138.87, -3.65) * mm, "mid": v(137.72, -3.88) * mm, "end": v(136.74, -4.53) * mm});
            skArc(sketch, "E278", {"start": v(136.74, 4.53) * mm, "mid": v(137.72, 3.88) * mm, "end": v(138.87, 3.65) * mm});
            skCircle(sketch, "E279", {"center": v(140, 0) * mm, "radius": 2.15 * mm});
            skArc(sketch, "E280", {"start": v(143.26, -4.53) * mm, "mid": v(142.28, -3.88) * mm, "end": v(141.13, -3.65) * mm});
            skArc(sketch, "E281", {"start": v(141.13, 3.65) * mm, "mid": v(142.28, 3.88) * mm, "end": v(143.26, 4.53) * mm});
            skArc(sketch, "E282", {"start": v(142.8, -8.2) * mm, "mid": v(142.59, -8.29) * mm, "end": v(142.5, -8.5) * mm});
            skArc(sketch, "E283", {"start": v(142.5, 8.5) * mm, "mid": v(142.59, 8.29) * mm, "end": v(142.8, 8.2) * mm});
            skArc(sketch, "E284", {"start": v(142.5, -9.2) * mm, "mid": v(142.73, -9.77) * mm, "end": v(143.3, -10) * mm});
            skArc(sketch, "E285", {"start": v(143.3, 10) * mm, "mid": v(142.73, 9.77) * mm, "end": v(142.5, 9.2) * mm});
            skArc(sketch, "E286", {"start": v(144.92, -8.2) * mm, "mid": v(145.69, -7.69) * mm, "end": v(145.5, -6.78) * mm});
            skArc(sketch, "E287", {"start": v(145.5, 6.78) * mm, "mid": v(145.69, 7.69) * mm, "end": v(144.92, 8.2) * mm});
            skArc(sketch, "E288", {"start": v(143.65, -1.13) * mm, "mid": v(143.88, -2.28) * mm, "end": v(144.53, -3.26) * mm});
            skArc(sketch, "E289", {"start": v(144.53, 3.26) * mm, "mid": v(143.88, 2.28) * mm, "end": v(143.65, 1.13) * mm});
            skArc(sketch, "E290", {"start": v(146.78, -5.5) * mm, "mid": v(147.69, -5.69) * mm, "end": v(148.2, -4.92) * mm});
            skArc(sketch, "E291", {"start": v(148.2, 4.92) * mm, "mid": v(147.69, 5.69) * mm, "end": v(146.78, 5.5) * mm});
            skArc(sketch, "E292", {"start": v(148, -10) * mm, "mid": v(149.41, -9.41) * mm, "end": v(150, -8) * mm});
            skArc(sketch, "E293", {"start": v(150, 8) * mm, "mid": v(149.41, 9.41) * mm, "end": v(148, 10) * mm});
            skArc(sketch, "E294", {"start": v(148.5, -2.5) * mm, "mid": v(148.29, -2.59) * mm, "end": v(148.2, -2.8) * mm});
            skArc(sketch, "E295", {"start": v(148.2, 2.8) * mm, "mid": v(148.29, 2.59) * mm, "end": v(148.5, 2.5) * mm});
            skArc(sketch, "E296", {"start": v(150, -3.3) * mm, "mid": v(149.77, -2.73) * mm, "end": v(149.2, -2.5) * mm});
            skArc(sketch, "E297", {"start": v(149.2, 2.5) * mm, "mid": v(149.77, 2.73) * mm, "end": v(150, 3.3) * mm});
            skLineSegment(sketch, "E298", {"start": v(140, 10) * mm, "end": v(140, -10) * mm});
            skLineSegment(sketch, "E299", {"start": v(130, 0) * mm, "end": v(150, 0) * mm});
            skSolve(sketch);
        }
        {
            var Q0;
            Q0 = qSketchRegion(id + "F2", true);
            extrude(context, id + "F3", {"entities" : qUnion([Q0]), "endBound" : BoundingType.SYMMETRIC, "depth" : 200 * mm});
        }
    });
